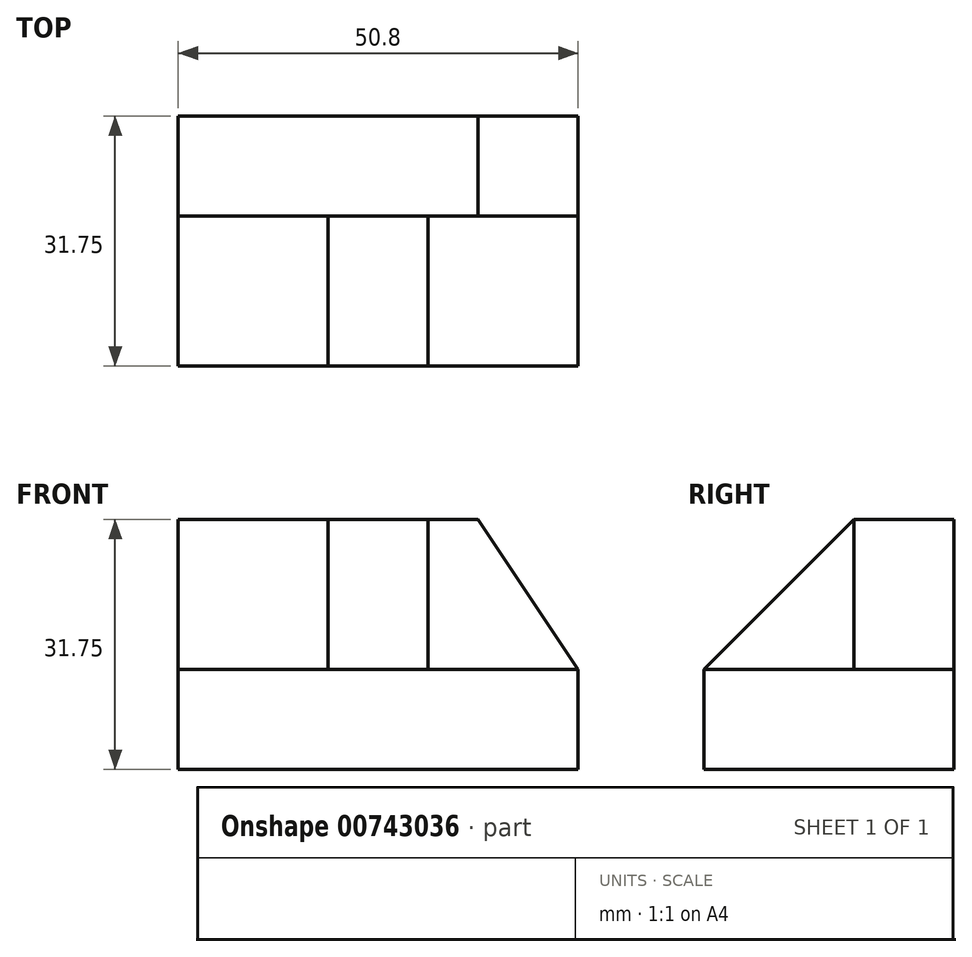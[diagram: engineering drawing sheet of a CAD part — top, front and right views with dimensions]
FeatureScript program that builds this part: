
annotation { "Feature Type Name" : "Feature", "Feature Type Description" : "" }
export const myFeature = defineFeature(function(context is Context, id is Id, definition is map)
    precondition{}
    {
        {
            var Q0;
            Q0=qCreatedBy(makeId("Front.planeOp"),FACE);
            var sketch = newSketch(context, id + "F0", { "sketchPlane" : qUnion([Q0])});
            skLineSegment(sketch, "E0", {"start": v(0, 0) * mm, "end": v(0, 31.75) * mm});
            skLineSegment(sketch, "E1", {"start": v(0, 31.75) * mm, "end": v(50.8, 31.75) * mm});
            skLineSegment(sketch, "E2", {"start": v(50.8, 31.75) * mm, "end": v(50.8, 0) * mm});
            skLineSegment(sketch, "E3", {"start": v(50.8, 0) * mm, "end": v(0, 0) * mm});
            skSolve(sketch);
        }
        {
            var Q0;
            Q0=makeQuery(id+"F0.imprint","IMPRINT",FACE,{"disambiguationData":[TD([[makeQuery(id+"F0.imprint","IMPRINT",EDGE,{"derivedFrom":sQuery(id+"F0.wireOp",EDGE,"E0")}),-1.0]])]});
            extrude(context, id + "F1", {"entities" : qUnion([Q0]), "depth" : 31.75 * mm, "offsetDistance" : 25.4 * mm});
        }
        {
            var Q0;
            Q0=makeQuery(id+"F1.opExtrude","SWEPT_FACE",FACE,{"disambiguationData":[OSD([sQuery(id+"F0.wireOp",EDGE,"E2")])]});
            var sketch = newSketch(context, id + "F2", { "sketchPlane" : qUnion([Q0])});
            skLineSegment(sketch, "E4.bottom", {"start": v(-31.75, 31.75) * mm, "end": v(-12.7, 31.75) * mm});
            skLineSegment(sketch, "E4.top", {"start": v(-31.75, 12.7) * mm, "end": v(-12.7, 12.7) * mm});
            skLineSegment(sketch, "E4.left", {"start": v(-31.75, 31.75) * mm, "end": v(-31.75, 12.7) * mm});
            skLineSegment(sketch, "E4.right", {"start": v(-12.7, 31.75) * mm, "end": v(-12.7, 12.7) * mm});
            skSolve(sketch);
        }
        {
            var Q0;
            Q0=makeQuery(id+"F2.imprint","IMPRINT",FACE,{"disambiguationData":[TD([[makeQuery(id+"F2.imprint","IMPRINT",EDGE,{"derivedFrom":sQuery(id+"F2.wireOp",EDGE,"E4.bottom")}),-1.0]])]});
            extrude(context, id + "F3", {"entities" : qUnion([Q0]), "operationType" : NewBodyOperationType.REMOVE, "oppositeDirection" : true, "depth" : 19.05 * mm, "offsetDistance" : 25.4 * mm});
        }
        {
            var Q0;
            Q0=makeQuery(id+"F1.opExtrude","SWEPT_FACE",FACE,{"disambiguationData":[OSD([sQuery(id+"F0.wireOp",EDGE,"E0")])]});
            var sketch = newSketch(context, id + "F4", { "sketchPlane" : qUnion([Q0])});
            skSolve(sketch);
        }
        {
            var Q0;
            {var subQ0=sQuery(id+"F0.wireOp",EDGE,"E0");Q0=makeQuery(id+"F4.imprint","IMPRINT",FACE,{"disambiguationData":[TD([[makeQuery(id+"F4.imprint","IMPRINT",EDGE,{"derivedFrom":makeQuery(id+"F1.opExtrude","CAP_EDGE",EDGE,{"disambiguationData":[OSD([subQ0])],"isStart":true})}),-1.0]])]});}
            var sketch = newSketch(context, id + "F5", { "sketchPlane" : qUnion([Q0])});
            skLineSegment(sketch, "E5.bottom", {"start": v(31.75, 31.75) * mm, "end": v(12.7, 31.75) * mm});
            skLineSegment(sketch, "E5.top", {"start": v(31.75, 12.7) * mm, "end": v(12.7, 12.7) * mm});
            skLineSegment(sketch, "E5.left", {"start": v(31.75, 31.75) * mm, "end": v(31.75, 12.7) * mm});
            skLineSegment(sketch, "E5.right", {"start": v(12.7, 31.75) * mm, "end": v(12.7, 12.7) * mm});
            skSolve(sketch);
        }
        {
            var Q0;
            Q0 = qSketchRegion(id + "F5", true);
            extrude(context, id + "F6", {"entities" : qUnion([Q0]), "operationType" : NewBodyOperationType.REMOVE, "oppositeDirection" : true, "depth" : 19.05 * mm, "offsetDistance" : 25.4 * mm});
        }
        {
            var Q0;
            Q0=makeQuery(id+"F3.boolean.opBoolean","COPY",FACE,{"derivedFrom":makeQuery(id+"F3.opExtrude","CAP_FACE",FACE,{"disambiguationData":[OSD([sQuery(id+"F2.wireOp",EDGE,"E4.bottom"),sQuery(id+"F2.wireOp",EDGE,"E4.top"),sQuery(id+"F2.wireOp",EDGE,"E4.left"),sQuery(id+"F2.wireOp",EDGE,"E4.right")])],"isStart":false})});
            var sketch = newSketch(context, id + "F7", { "sketchPlane" : qUnion([Q0])});
            skLineSegment(sketch, "E6", {"start": v(-31.75, 12.7) * mm, "end": v(-12.7, 31.75) * mm});
            skLineSegment(sketch, "E7", {"start": v(-12.7, 31.75) * mm, "end": v(-31.75, 31.75) * mm});
            skLineSegment(sketch, "E8", {"start": v(-31.75, 31.75) * mm, "end": v(-31.75, 12.7) * mm});
            skSolve(sketch);
        }
        {
            var Q0;
            Q0 = qSketchRegion(id + "F7", true);
            extrude(context, id + "F8", {"entities" : qUnion([Q0]), "operationType" : NewBodyOperationType.REMOVE, "oppositeDirection" : true, "depth" : 25.4 * mm, "offsetDistance" : 25.4 * mm});
        }
        {
            var Q0;
            Q0=makeQuery(id+"F3.boolean.opBoolean","COPY",FACE,{"derivedFrom":makeQuery(id+"F3.opExtrude","SWEPT_FACE",FACE,{"disambiguationData":[OSD([sQuery(id+"F2.wireOp",EDGE,"E4.right")])]})});
            var sketch = newSketch(context, id + "F9", { "sketchPlane" : qUnion([Q0])});
            skLineSegment(sketch, "E9", {"start": v(50.8, 12.7) * mm, "end": v(31.75, 12.7) * mm});
            skLineSegment(sketch, "E10", {"start": v(31.75, 12.7) * mm, "end": v(31.75, 31.75) * mm});
            skLineSegment(sketch, "E11", {"start": v(31.75, 31.75) * mm, "end": v(38.1, 31.75) * mm});
            skLineSegment(sketch, "E12", {"start": v(38.1, 31.75) * mm, "end": v(50.8, 12.7) * mm});
            skSolve(sketch);
        }
        {
            var Q0;
            {var subQ0=sQuery(id+"F9.wireOp",EDGE,"E12");Q0=makeQuery(id+"F9.imprint","IMPRINT",FACE,{"disambiguationData":[TD([[makeQuery(id+"F9.imprint","IMPRINT",EDGE,{"derivedFrom":subQ0}),1.0]])]});}
            extrude(context, id + "F10", {"entities" : qUnion([Q0]), "operationType" : NewBodyOperationType.REMOVE, "oppositeDirection" : true, "depth" : 25.4 * mm, "offsetDistance" : 25.4 * mm});
        }
    });
